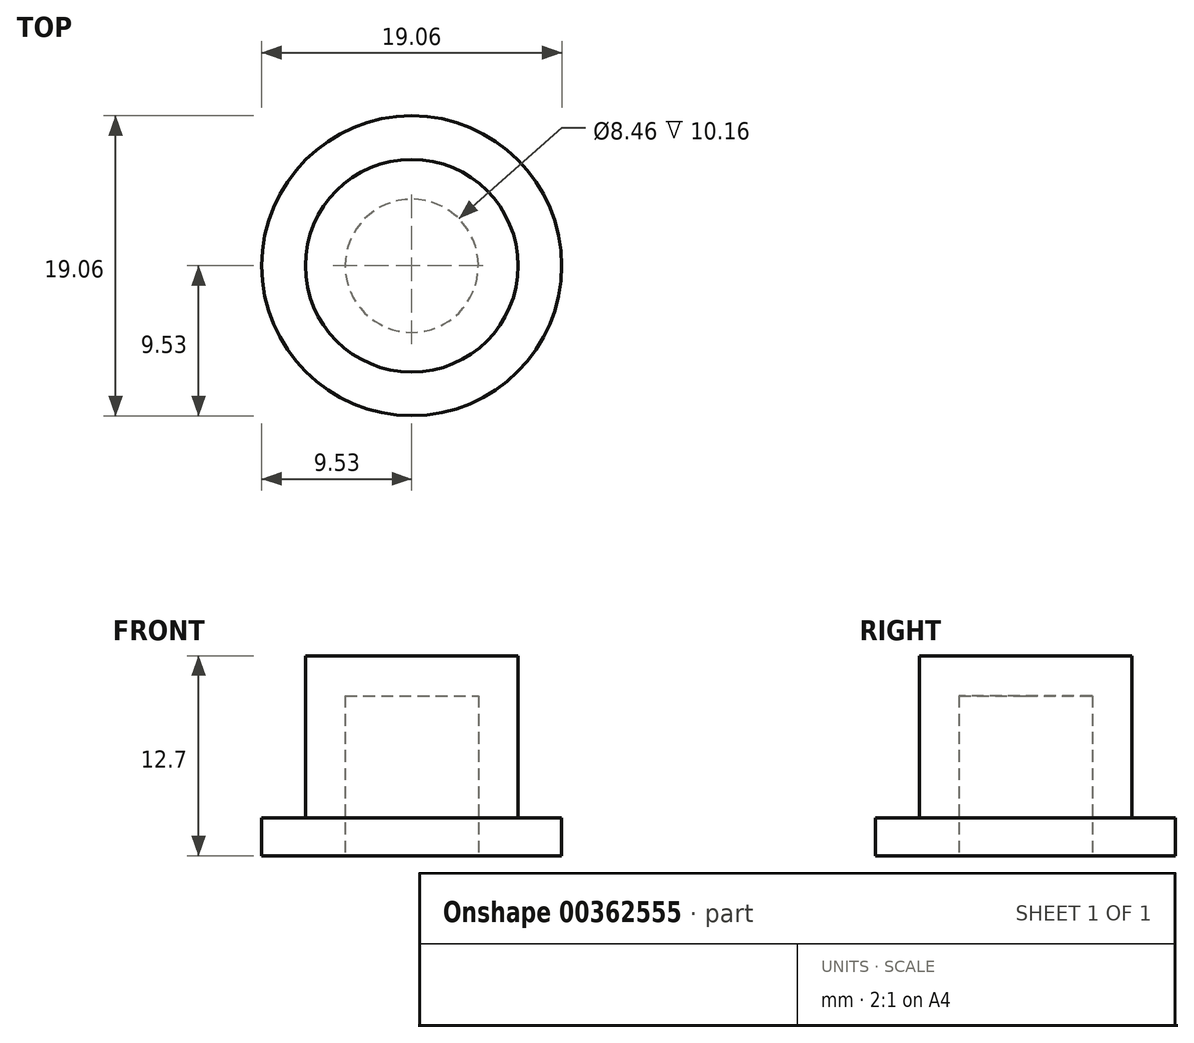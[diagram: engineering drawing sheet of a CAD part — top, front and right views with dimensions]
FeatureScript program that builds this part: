
annotation { "Feature Type Name" : "Feature", "Feature Type Description" : "" }
export const myFeature = defineFeature(function(context is Context, id is Id, definition is map)
    precondition{}
    {
        {
            var Q0;
            Q0=qCreatedBy(makeId("Front.planeOp"),FACE);
            var sketch = newSketch(context, id + "F0", { "sketchPlane" : qUnion([Q0])});
            skLineSegment(sketch, "E0.top", {"start": v(0, 12.7) * mm, "end": v(6.76, 12.7) * mm});
            skLineSegment(sketch, "E0.left", {"start": v(0, 0) * mm, "end": v(0, 12.7) * mm});
            skLineSegment(sketch, "E0.right", {"start": v(6.76, 2.41) * mm, "end": v(6.76, 12.7) * mm});
            skLineSegment(sketch, "E1.top", {"start": v(6.76, 2.41) * mm, "end": v(9.53, 2.41) * mm});
            skLineSegment(sketch, "E1.right", {"start": v(9.53, 0) * mm, "end": v(9.53, 2.41) * mm});
            skLineSegment(sketch, "E2", {"start": v(0, 0) * mm, "end": v(9.53, 0) * mm});
            skSolve(sketch);
        }
        {
            var Q0;
            Q0=makeQuery(id+"F0.imprint","IMPRINT",FACE,{"disambiguationData":[TD([[makeQuery(id+"F0.imprint","IMPRINT",EDGE,{"derivedFrom":sQuery(id+"F0.wireOp",EDGE,"E0.top")}),-1.0]])]});
            var Q1;
            Q1=sQuery(id+"F0.wireOp",EDGE,"E0.left");
            revolve(context, id + "F1", {"entities" : qUnion([Q0]), "axis" : qUnion([Q1]), "revolveType" : RevolveType.FULL});
        }
        {
            var Q0;
            Q0=makeQuery(id+"F1.opRevolve","SWEPT_FACE",FACE,{"disambiguationData":[OSD([sQuery(id+"F0.wireOp",EDGE,"E2")])]});
            var sketch = newSketch(context, id + "F2", { "sketchPlane" : qUnion([Q0])});
            skCircle(sketch, "E3", {"center": v(0, 0) * mm, "radius": 4.23 * mm});
            skSolve(sketch);
        }
        {
            var Q0;
            Q0=makeQuery(id+"F2.imprint","IMPRINT",FACE,{"disambiguationData":[TD([[makeQuery(id+"F2.imprint","IMPRINT",EDGE,{"derivedFrom":sQuery(id+"F2.wireOp",EDGE,"E3")}),1.0]])]});
            extrude(context, id + "F3", {"entities" : qUnion([Q0]), "operationType" : NewBodyOperationType.REMOVE, "oppositeDirection" : true, "depth" : 10.16 * mm});
        }
    });
